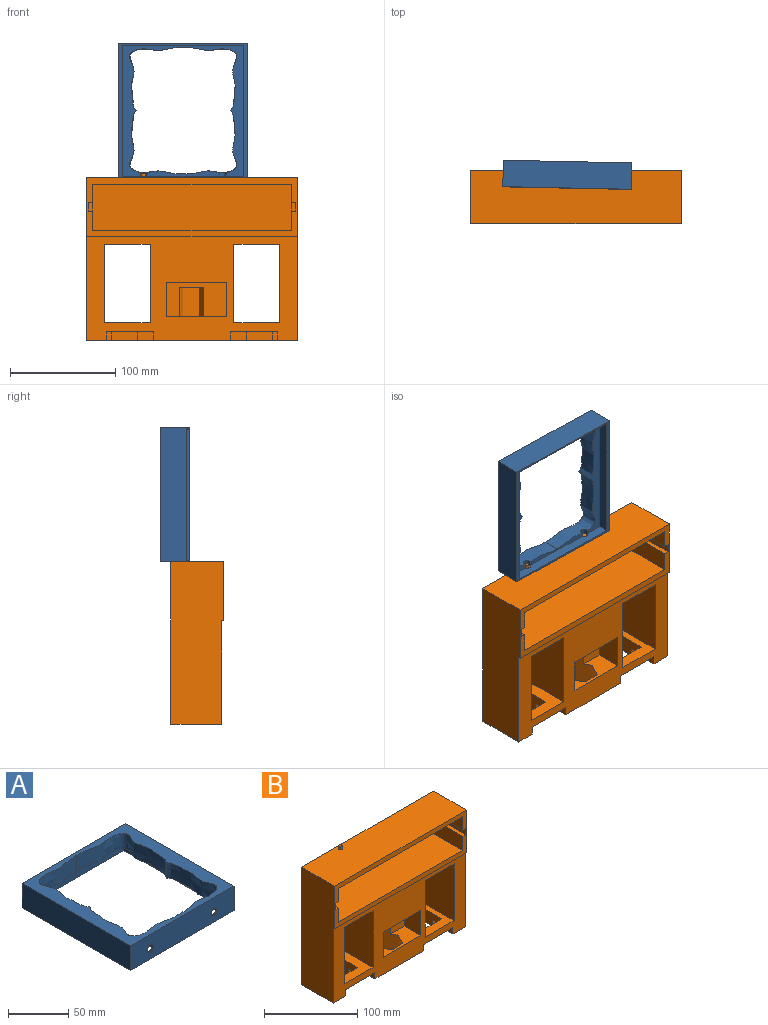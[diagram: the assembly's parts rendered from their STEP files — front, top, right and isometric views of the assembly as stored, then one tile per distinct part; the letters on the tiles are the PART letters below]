
ASSEMBLY  parts=2 mates=1
PART A: 18 faces, bbox 121.8x127.2x25 mm
  f0: plane 124.25x114.75mm, normal (0,0,-1), area 2660.7mm2, adj f1,f4,f9,f10,f12,f13,f14,f15
  f1: extruded ~59.99x50.9mm, area 1653.6mm2, adj f0,f2,f4,f5,f9,f16
  f2: plane 68.63x5.24mm, normal (0,0,-1), area 244.7mm2, adj f1,f4,f15,f16,f17
  f3: plane 127.24x121.75mm, normal (0,0,-1), area 1235mm2, adj f6,f7,f8,f11,f12,f13,f14,f15
  f4: extruded ~59.99x50.9mm, area 1653.6mm2, adj f0,f1,f2,f5,f10,f17
  f5: plane 127.24x121.75mm, normal (0,0,1), area 4187.6mm2, adj f1,f4,f6,f7,f8,f9,f10,f11
  f6: plane 127.24x25mm, normal (1,0,0), area 3181.1mm2, adj f3,f5,f7,f11
  f7: plane 121.75x25mm, normal (0,1,0), area 3043.7mm2, adj f3,f5,f6,f8
  f8: plane 127.24x25mm, normal (-1,0,0), area 3181.1mm2, adj f3,f5,f7,f11
  f9: extruded ~59.99x50.9mm, area 1680.6mm2, adj f0,f1,f5,f10
  f10: extruded ~59.99x50.9mm, area 1680.6mm2, adj f0,f4,f5,f9
  f11: plane 121.75x25mm, normal (0,-1,0), area 2966.8mm2, adj f3,f5,f6,f8,f16,f17
  f12: plane 124.25x9.4mm, normal (-1,0,0), area 1167.9mm2, adj f0,f3,f13,f15
  f13: plane 114.75x9.4mm, normal (0,-1,0), area 1078.6mm2, adj f0,f3,f12,f14
  f14: plane 124.25x9.4mm, normal (1,0,0), area 1167.9mm2, adj f0,f3,f13,f15
  f15: plane 114.75x9.4mm, normal (0,1,0), area 1055.3mm2, adj f0,f2,f3,f12,f14,f16,f17
  f16: cylinder r=3.5mm len=7mm, axis (0,1,0), area 80.8mm2, adj f0,f1,f2,f11,f15
  f17: cylinder r=3.5mm len=7mm, axis (0,1,0), area 80.8mm2, adj f0,f2,f4,f11,f15
PART B: 61 faces, bbox 200x50x157.9 mm
  f0: plane 200x98.2mm, normal (0,-1,0), area 10575.9mm2, adj f2,f3,f5,f7,f9,f11,f13,f29
  f1: plane 22.8x6.15mm, normal (0,0,-1), area 112.6mm2, adj f52,f53,f54,f60
  f2: plane 200x48.09mm, normal (0,0,-1), area 6132mm2, adj f0,f4,f6,f8,f11,f13,f29,f30
  f3: plane 44.7x25mm, normal (0,0,-1), area 793.6mm2, adj f0,f4,f39,f40,f41,f46,f47,f49
  f4: plane 8.1x5.55mm, normal (0,-1,0), area 44.9mm2, adj f2,f3,f40,f47
  f5: plane 44.7x25mm, normal (0,0,-1), area 793.6mm2, adj f0,f6,f29,f30,f31,f35,f36,f38
  f6: plane 15.02x8.1mm, normal (0,-1,0), area 121.7mm2, adj f2,f5,f30,f36
  f7: plane 48.09x43.4mm, normal (0,0,1), area 1473.2mm2, adj f0,f8,f32,f34,f35,f36,f37,f38
  f8: plane 200x154.2mm, normal (0,1,0), area 24383.1mm2, adj f2,f7,f11,f12,f13,f32,f33,f34
  f9: plane 200x1.91mm, normal (0,0,-1), area 382.9mm2, adj f0,f10,f11,f13
  f10: plane 200x56mm, normal (0,-1,0), area 2854.1mm2, adj f9,f11,f12,f13,f14,f15,f16,f17
  f11: plane 154.2x50mm, normal (1,0,0), area 7522mm2, adj f0,f2,f8,f9,f10,f12
  f12: plane 200x50mm, normal (0,0,1), area 9985.5mm2, adj f8,f10,f11,f13,f27
  f13: plane 154.2x50mm, normal (-1,0,0), area 7522mm2, adj f0,f2,f8,f9,f10,f12
  f14: plane 44x44mm, normal (-1,0,0), area 1586.6mm2, adj f10,f15,f17,f18,f23,f24,f25
  f15: plane 188x44mm, normal (0,0,-1), area 8272mm2, adj f10,f14,f16,f18
  f16: plane 44x44mm, normal (1,0,0), area 1586.6mm2, adj f10,f15,f17,f18,f19,f20,f21
  f17: plane 188x44mm, normal (0,0,1), area 8272mm2, adj f10,f14,f16,f18
  f18: plane 188x44mm, normal (0,-1,0), area 8272mm2, adj f14,f15,f16,f17
  f19: plane 42.1x4.4mm, normal (0,0,-1), area 185.2mm2, adj f10,f16,f20,f22
  f20: plane 8.3x4.4mm, normal (0,-1,0), area 36.5mm2, adj f16,f19,f21,f22
  f21: plane 42.1x4.4mm, normal (0,0,1), area 185.2mm2, adj f10,f16,f20,f22
  f22: plane 42.1x8.3mm, normal (1,0,0), area 349.4mm2, adj f10,f19,f20,f21
  f23: plane 42.1x4.5mm, normal (0,0,1), area 189.4mm2, adj f10,f14,f24,f26
  f24: plane 8.3x4.5mm, normal (0,-1,0), area 37.4mm2, adj f14,f23,f25,f26
  f25: plane 42.1x4.5mm, normal (0,0,-1), area 189.4mm2, adj f10,f14,f24,f26
  f26: plane 42.1x8.3mm, normal (-1,0,0), area 349.4mm2, adj f10,f23,f24,f25
  f27: cylinder r=2.15mm len=4.3mm, axis (0,0,-1), area 49.9mm2, adj f12,f28
  f28: plane 4.3x4.3mm, normal (0,0,1), area 14.5mm2, adj f27
  f29: plane 25x8.1mm, normal (1,0,0), area 202.5mm2, adj f0,f2,f5,f31
  f30: plane 25x8.1mm, normal (-1,0,0), area 202.5mm2, adj f0,f2,f5,f6
  f31: plane 8.1x5.55mm, normal (0,-1,0), area 44.9mm2, adj f2,f5,f29,f38
  f32: plane 74.39x48.09mm, normal (-1,0,0), area 3577.3mm2, adj f0,f7,f8,f33
  f33: plane 48.09x43.4mm, normal (0,0,-1), area 2086.7mm2, adj f0,f8,f32,f34
  f34: plane 74.39x48.09mm, normal (1,0,0), area 3577.3mm2, adj f0,f7,f8,f33
  f35: plane 24.13x8.45mm, normal (0,1,0), area 203.9mm2, adj f5,f7,f36,f38
  f36: plane 25.43x16.55mm, normal (-1,0,0), area 312.1mm2, adj f2,f5,f6,f7,f35,f37
  f37: plane 24.13x16.55mm, normal (0,-1,0), area 399.4mm2, adj f2,f7,f36,f38
  f38: plane 25.43x16.55mm, normal (1,0,0), area 312.1mm2, adj f2,f5,f7,f31,f35,f37
  f39: plane 25x8.1mm, normal (1,0,0), area 202.5mm2, adj f0,f2,f3,f41
  f40: plane 25x8.1mm, normal (-1,0,0), area 202.5mm2, adj f0,f2,f3,f4
  f41: plane 15.02x8.1mm, normal (0,-1,0), area 121.7mm2, adj f2,f3,f39,f49
  f42: plane 74.39x48.09mm, normal (1,0,0), area 3577.3mm2, adj f0,f8,f43,f45
  f43: plane 48.09x43.4mm, normal (0,0,1), area 1473.2mm2, adj f0,f8,f42,f44,f46,f47,f48,f49
  f44: plane 74.39x48.09mm, normal (-1,0,0), area 3577.3mm2, adj f0,f8,f43,f45
  f45: plane 48.09x43.4mm, normal (0,0,-1), area 2086.7mm2, adj f0,f8,f42,f44
  f46: plane 24.13x8.45mm, normal (0,1,0), area 203.9mm2, adj f3,f43,f47,f49
  f47: plane 25.43x16.55mm, normal (-1,0,0), area 312.1mm2, adj f2,f3,f4,f43,f46,f48
  f48: plane 24.13x16.55mm, normal (0,-1,0), area 399.4mm2, adj f2,f43,f47,f49
  f49: plane 25.43x16.55mm, normal (1,0,0), area 312.1mm2, adj f2,f3,f41,f43,f46,f48
  f50: plane 22.27x16.05mm, normal (-0.05,1,0), area 357.8mm2, adj f2,f51,f55,f58
  f51: plane 22.27x13.53mm, normal (0.84,0.54,0), area 357.8mm2, adj f2,f50,f52,f58
  f52: plane 50.3x14.27mm, normal (0.89,-0.46,0), area 528.9mm2, adj f1,f2,f51,f53,f58,f60
  f53: plane 50.3x16.05mm, normal (0.05,-1,0), area 808.1mm2, adj f1,f2,f52,f54
  f54: plane 50.3x13.53mm, normal (-0.84,-0.54,0), area 562.6mm2, adj f1,f2,f53,f55,f58,f60
  f55: plane 22.27x14.27mm, normal (-0.89,0.46,0), area 357.8mm2, adj f2,f50,f54,f58
  f56: plane 57.23x25mm, normal (0,0,-1), area 1430.7mm2, adj f0,f57,f59,f60
  f57: plane 32.91x25mm, normal (1,0,0), area 822.6mm2, adj f0,f56,f58,f60
  f58: plane 57.23x25mm, normal (0,0,1), area 872.6mm2, adj f0,f50,f51,f52,f54,f55,f57,f59
  f59: plane 32.91x25mm, normal (-1,0,0), area 822.6mm2, adj f0,f56,f58,f60
  f60: plane 57.23x32.91mm, normal (0,-1,0), area 1244.1mm2, adj f1,f52,f54,f56,f57,f58,f59
PLACE A rot(axis=(0.01,0.71,0.71),179.2deg) t=(-8.53,-88.35,91.63)mm
PLACE B t=(0,-72,0)mm fixed
MATE pin_slot B.f27 <-> A.f16  axis (0,0,1) through (-46.31,-77.07,28)mm
